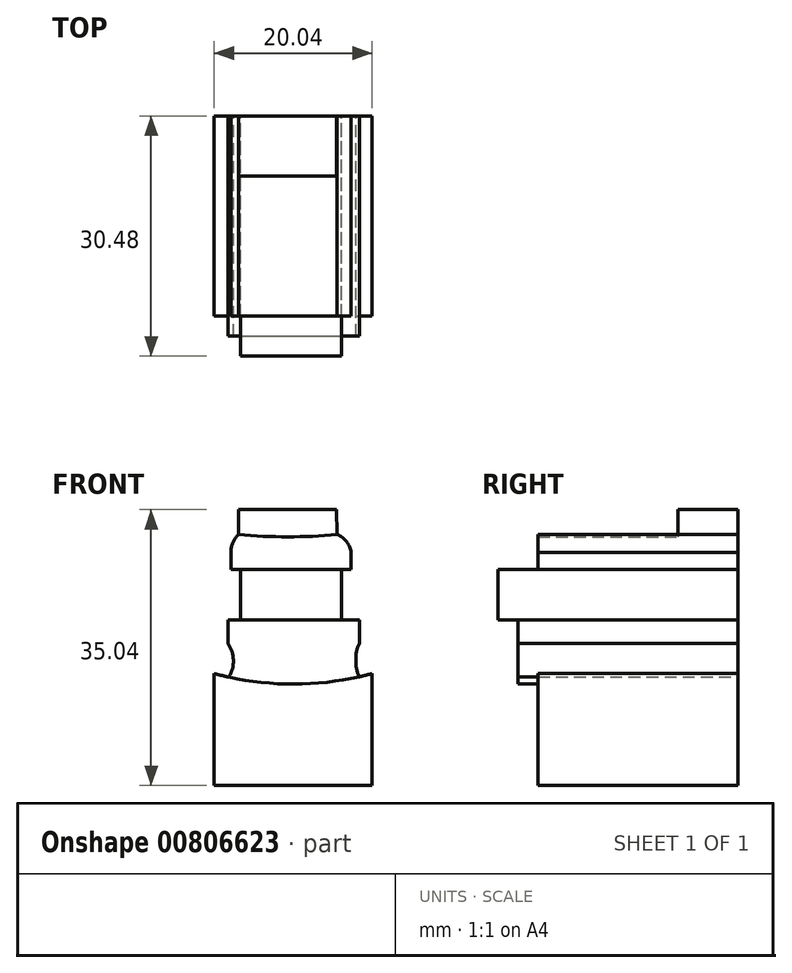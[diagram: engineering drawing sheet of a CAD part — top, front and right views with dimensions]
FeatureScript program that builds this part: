
annotation { "Feature Type Name" : "Feature", "Feature Type Description" : "" }
export const myFeature = defineFeature(function(context is Context, id is Id, definition is map)
    precondition{}
    {
        {
            var Q0;
            Q0=qCreatedBy(makeId("Front.planeOp"),FACE);
            var sketch = newSketch(context, id + "F0", { "sketchPlane" : qUnion([Q0])});
            skLineSegment(sketch, "E0.bottom", {"start": v(0, 0) * mm, "end": v(-20.04, 0) * mm});
            skLineSegment(sketch, "E0.left", {"start": v(0, 0) * mm, "end": v(0, 14.2) * mm});
            skLineSegment(sketch, "E0.right", {"start": v(-20.04, 0) * mm, "end": v(-20.04, 14.2) * mm});
            skArc(sketch, "E1", {"start": v(-20.04, 14.2) * mm, "mid": v(-10.02, 12.87) * mm, "end": v(0, 14.2) * mm});
            skLineSegment(sketch, "E2", {"start": v(-18.32, 18.04) * mm, "end": v(-18.32, 21.02) * mm});
            skLineSegment(sketch, "E3", {"start": v(-18.32, 21.02) * mm, "end": v(-1.62, 21.02) * mm});
            skLineSegment(sketch, "E4", {"start": v(-1.62, 21.02) * mm, "end": v(-1.62, 18.04) * mm});
            skArc(sketch, "E5", {"start": v(-18.32, 13.56) * mm, "mid": v(-17.6, 15.8) * mm, "end": v(-18.32, 18.04) * mm});
            skArc(sketch, "E6", {"start": v(-1.62, 18.04) * mm, "mid": v(-2.07, 15.92) * mm, "end": v(-1.62, 13.8) * mm});
            skPoint(sketch, "E7.end.orphan", {"position": v(-17.3, 18.04) * mm});
            skPoint(sketch, "E7.start.orphan", {"position": v(-17.3, 13.56) * mm});
            skLineSegment(sketch, "E8", {"start": v(-16.68, 21.02) * mm, "end": v(-16.68, 27.41) * mm});
            skLineSegment(sketch, "E9", {"start": v(-16.68, 27.41) * mm, "end": v(-3.88, 27.41) * mm});
            skLineSegment(sketch, "E10", {"start": v(-3.88, 27.41) * mm, "end": v(-3.88, 21.02) * mm});
            skLineSegment(sketch, "E11", {"start": v(-16.68, 27.41) * mm, "end": v(-17.94, 27.41) * mm});
            skLineSegment(sketch, "E12", {"start": v(-17.94, 27.41) * mm, "end": v(-17.94, 29.64) * mm});
            skLineSegment(sketch, "E13", {"start": v(-2.65, 29.59) * mm, "end": v(-2.65, 27.41) * mm});
            skLineSegment(sketch, "E14", {"start": v(-2.65, 27.41) * mm, "end": v(-3.88, 27.41) * mm});
            skArc(sketch, "E15", {"start": v(-16.99, 31.86) * mm, "mid": v(-17.68, 30.84) * mm, "end": v(-17.94, 29.64) * mm});
            skPoint(sketch, "E16.orphan", {"position": v(-17.94, 31.86) * mm});
            skArc(sketch, "E17", {"start": v(-2.65, 29.59) * mm, "mid": v(-3.23, 30.97) * mm, "end": v(-4.44, 31.86) * mm});
            skPoint(sketch, "E17.startSnap0", {"position": v(-2.65, 28.97) * mm});
            skPoint(sketch, "E18.orphan", {"position": v(-2.65, 30.52) * mm});
            skArc(sketch, "E19", {"start": v(-16.99, 31.86) * mm, "mid": v(-10.71, 31.58) * mm, "end": v(-4.44, 31.86) * mm});
            skPoint(sketch, "E20.end.orphan", {"position": v(-4.97, 31.86) * mm});
            skPoint(sketch, "E21.end.orphan", {"position": v(-5.38, 31.86) * mm});
            skLineSegment(sketch, "E22", {"start": v(-16.99, 31.86) * mm, "end": v(-16.99, 34.04) * mm});
            skLineSegment(sketch, "E23", {"start": v(-16.99, 34.04) * mm, "end": v(-16.99, 35.04) * mm});
            skLineSegment(sketch, "E24", {"start": v(-16.99, 35.04) * mm, "end": v(-4.5, 35.04) * mm});
            skLineSegment(sketch, "E25", {"start": v(-4.5, 35.04) * mm, "end": v(-4.44, 31.86) * mm});
            skSolve(sketch);
        }
        {
            var Q0;
            Q0=makeQuery(id+"F0.imprint","IMPRINT",FACE,{"disambiguationData":[TD([[makeQuery(id+"F0.imprint","IMPRINT",EDGE,{"derivedFrom":sQuery(id+"F0.wireOp",EDGE,"E0.bottom")}),-1.0]])]});
            extrude(context, id + "F1", {"entities" : qUnion([Q0]), "depth" : 25.4 * mm, "offsetDistance" : 25.4 * mm});
        }
        {
            var Q0;
            {var subQ3=sQuery(id+"F0.wireOp",EDGE,"E2");Q0=makeQuery(id+"F0.imprint","IMPRINT",FACE,{"disambiguationData":[TD([[makeQuery(id+"F0.imprint","IMPRINT",EDGE,{"derivedFrom":subQ3}),-1.0]])]});}
            extrude(context, id + "F2", {"entities" : qUnion([Q0]), "operationType" : NewBodyOperationType.ADD, "depth" : 27.94 * mm, "offsetDistance" : 25.4 * mm});
        }
        {
            var Q0;
            {var subQ0=sQuery(id+"F0.wireOp",EDGE,"E8");Q0=makeQuery(id+"F0.imprint","IMPRINT",FACE,{"disambiguationData":[TD([[makeQuery(id+"F0.imprint","IMPRINT",EDGE,{"derivedFrom":subQ0}),-1.0]])]});}
            extrude(context, id + "F3", {"entities" : qUnion([Q0]), "operationType" : NewBodyOperationType.ADD, "depth" : 30.48 * mm, "offsetDistance" : 25.4 * mm});
        }
        {
            var Q0;
            Q0=makeQuery(id+"F0.imprint","IMPRINT",FACE,{"disambiguationData":[TD([[makeQuery(id+"F0.imprint","IMPRINT",EDGE,{"derivedFrom":sQuery(id+"F0.wireOp",EDGE,"E9")}),1.0]])]});
            extrude(context, id + "F4", {"entities" : qUnion([Q0]), "operationType" : NewBodyOperationType.ADD, "depth" : 25.4 * mm, "offsetDistance" : 25.4 * mm});
        }
        {
            var Q0;
            Q0=makeQuery(id+"F0.imprint","IMPRINT",FACE,{"disambiguationData":[TD([[makeQuery(id+"F0.imprint","IMPRINT",EDGE,{"derivedFrom":sQuery(id+"F0.wireOp",EDGE,"E19")}),1.0]])]});
            extrude(context, id + "F5", {"entities" : qUnion([Q0]), "operationType" : NewBodyOperationType.ADD, "depth" : 7.62 * mm, "offsetDistance" : 25.4 * mm});
        }
    });
